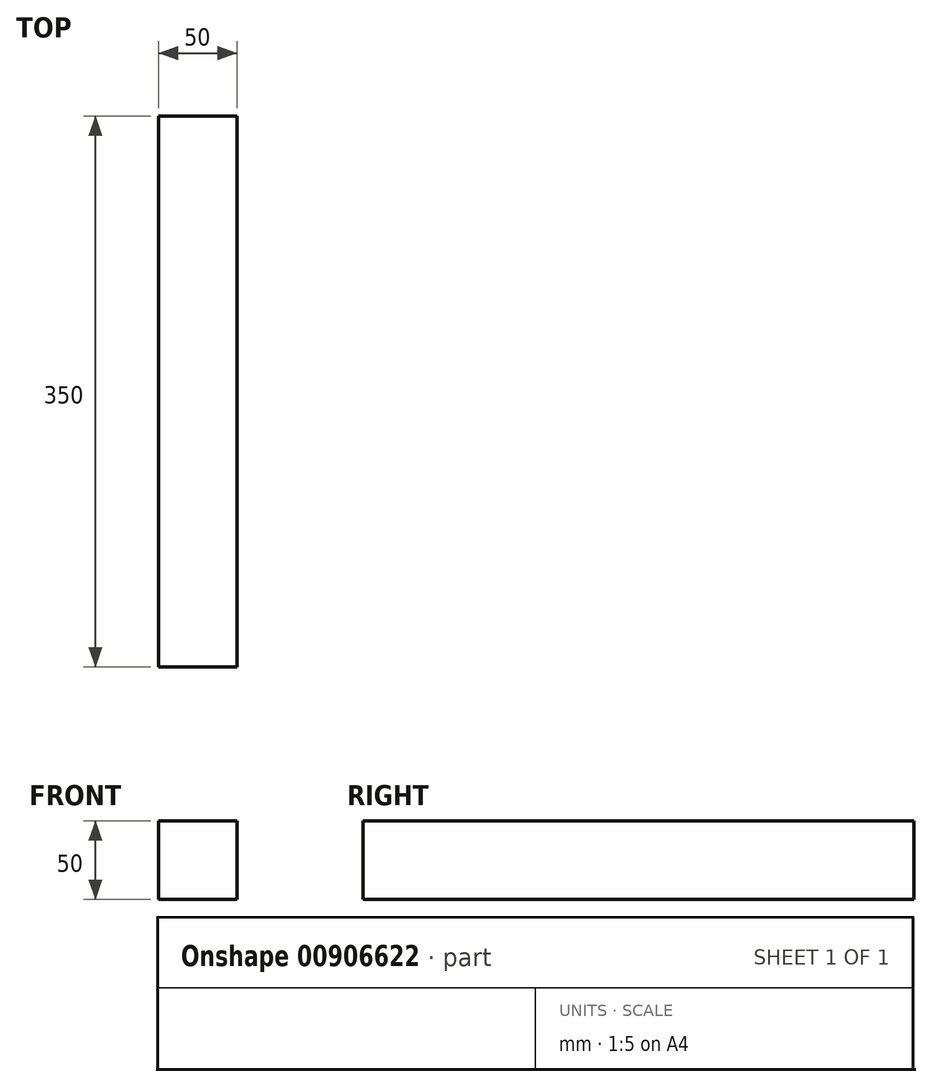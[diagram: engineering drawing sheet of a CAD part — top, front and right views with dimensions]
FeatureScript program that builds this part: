
annotation { "Feature Type Name" : "Feature", "Feature Type Description" : "" }
export const myFeature = defineFeature(function(context is Context, id is Id, definition is map)
    precondition{}
    {
        {
            var Q0;
            Q0=qCreatedBy(makeId("Front.planeOp"),FACE);
            var sketch = newSketch(context, id + "F0", { "sketchPlane" : qUnion([Q0])});
            skLineSegment(sketch, "E0.bottom", {"start": v(25, -25) * mm, "end": v(-25, -25) * mm});
            skLineSegment(sketch, "E0.top", {"start": v(25, 25) * mm, "end": v(-25, 25) * mm});
            skLineSegment(sketch, "E0.left", {"start": v(25, -25) * mm, "end": v(25, 25) * mm});
            skLineSegment(sketch, "E0.right", {"start": v(-25, -25) * mm, "end": v(-25, 25) * mm});
            skPoint(sketch, "E0.middle", {"position": v(0, 0) * mm});
            skSolve(sketch);
        }
        {
            var Q0;
            Q0=makeQuery(id+"F0.imprint","IMPRINT",FACE,{"disambiguationData":[TD([[makeQuery(id+"F0.imprint","IMPRINT",EDGE,{"derivedFrom":sQuery(id+"F0.wireOp",EDGE,"E0.bottom")}),-1.0]])]});
            extrude(context, id + "F1", {"entities" : qUnion([Q0]), "depth" : 350 * mm, "offsetDistance" : 25 * mm});
        }
    });
